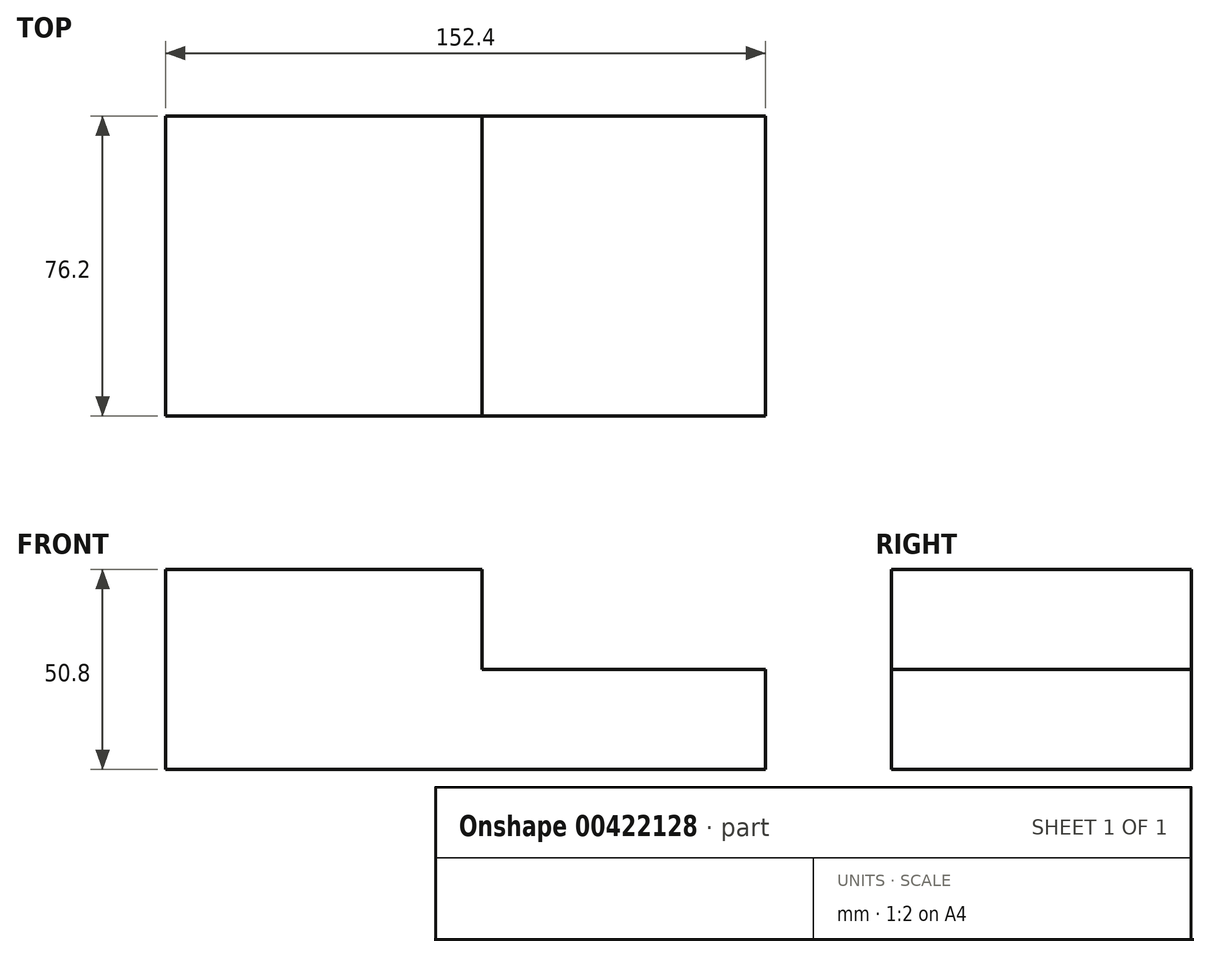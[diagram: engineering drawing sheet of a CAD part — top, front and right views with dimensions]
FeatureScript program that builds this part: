
annotation { "Feature Type Name" : "Feature", "Feature Type Description" : "" }
export const myFeature = defineFeature(function(context is Context, id is Id, definition is map)
    precondition{}
    {
        {
            var Q0;
            Q0=qCreatedBy(makeId("Front.planeOp"),FACE);
            var sketch = newSketch(context, id + "F0", { "sketchPlane" : qUnion([Q0])});
            skLineSegment(sketch, "E0", {"start": v(0, 0) * mm, "end": v(152.4, 0) * mm});
            skLineSegment(sketch, "E1", {"start": v(152.4, 25.4) * mm, "end": v(152.4, 0) * mm});
            skLineSegment(sketch, "E2", {"start": v(80.36, 25.4) * mm, "end": v(152.4, 25.4) * mm});
            skLineSegment(sketch, "E3", {"start": v(80.36, 25.4) * mm, "end": v(80.36, 50.8) * mm});
            skLineSegment(sketch, "E4", {"start": v(80.36, 50.8) * mm, "end": v(0, 50.8) * mm});
            skLineSegment(sketch, "E5", {"start": v(0, 50.8) * mm, "end": v(0, 0) * mm});
            skSolve(sketch);
        }
        {
            var Q0;
            Q0=makeQuery(id+"F0.imprint","IMPRINT",FACE,{"disambiguationData":[TD([[makeQuery(id+"F0.imprint","IMPRINT",EDGE,{"derivedFrom":sQuery(id+"F0.wireOp",EDGE,"E0")}),1.0]])]});
            extrude(context, id + "F1", {"entities" : qUnion([Q0]), "depth" : 76.2 * mm});
        }
    });
